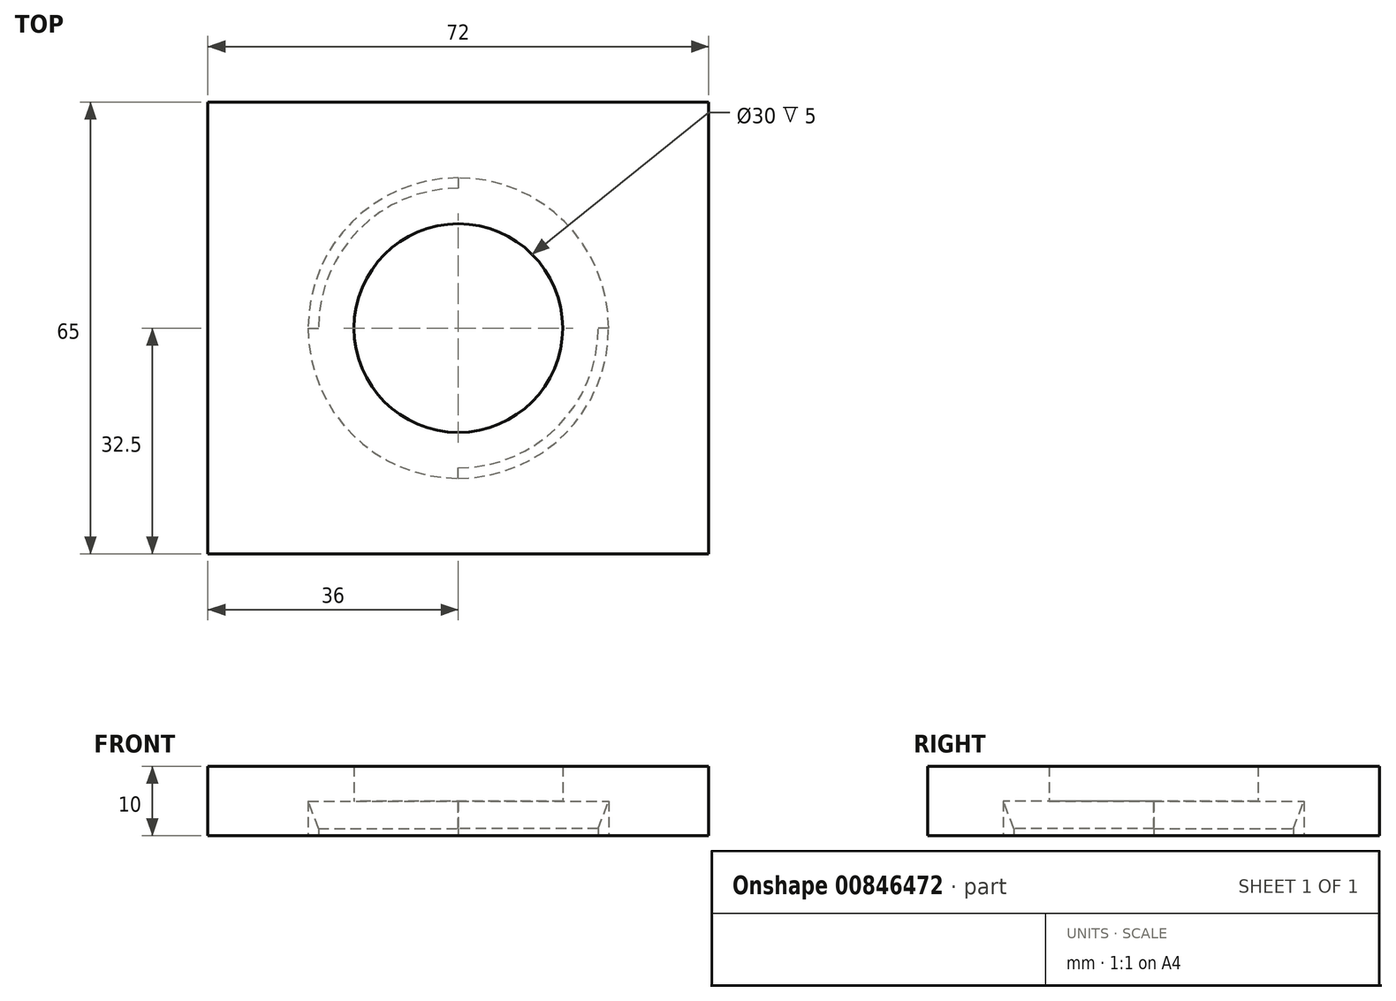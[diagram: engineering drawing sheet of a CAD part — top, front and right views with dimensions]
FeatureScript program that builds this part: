
annotation { "Feature Type Name" : "Feature", "Feature Type Description" : "" }
export const myFeature = defineFeature(function(context is Context, id is Id, definition is map)
    precondition{}
    {
        {
            var Q0;
            Q0=qCreatedBy(makeId("Top.planeOp"),FACE);
            var sketch = newSketch(context, id + "F0", { "sketchPlane" : qUnion([Q0])});
            skLineSegment(sketch, "E0.bottom", {"start": v(36, -32.5) * mm, "end": v(-36, -32.5) * mm});
            skLineSegment(sketch, "E0.top", {"start": v(36, 32.5) * mm, "end": v(-36, 32.5) * mm});
            skLineSegment(sketch, "E0.left", {"start": v(36, -32.5) * mm, "end": v(36, 32.5) * mm});
            skLineSegment(sketch, "E0.right", {"start": v(-36, -32.5) * mm, "end": v(-36, 32.5) * mm});
            skPoint(sketch, "E0.middle", {"position": v(0, 0) * mm});
            skCircle(sketch, "E1", {"center": v(0, 0) * mm, "radius": 15 * mm});
            skSolve(sketch);
        }
        {
            var Q0;
            Q0=makeQuery(id+"F0.imprint","IMPRINT",FACE,{"disambiguationData":[TD([[makeQuery(id+"F0.imprint","IMPRINT",EDGE,{"derivedFrom":sQuery(id+"F0.wireOp",EDGE,"E0.bottom")}),-1.0]])]});
            extrude(context, id + "F1", {"entities" : qUnion([Q0]), "depth" : 10 * mm, "offsetDistance" : 25 * mm});
        }
        {
            var Q0;
            Q0=qCreatedBy(makeId("Right.planeOp"),FACE);
            var sketch = newSketch(context, id + "F2", { "sketchPlane" : qUnion([Q0])});
            skLineSegment(sketch, "E2", {"start": v(0, 0) * mm, "end": v(-20.1, 0) * mm});
            skLineSegment(sketch, "E3", {"start": v(-20.1, 0) * mm, "end": v(-20.1, 1) * mm});
            skLineSegment(sketch, "E4", {"start": v(-20.1, 1) * mm, "end": v(-21.6, 5) * mm});
            skLineSegment(sketch, "E5", {"start": v(-21.6, 5) * mm, "end": v(0, 5) * mm});
            skLineSegment(sketch, "E6", {"start": v(0, 5) * mm, "end": v(0, 0) * mm});
            skSolve(sketch);
        }
        {
            var Q0;
            Q0 = qSketchRegion(id + "F2", true);
            var Q1;
            Q1=sQuery(id+"F2.wireOp",EDGE,"E6");
            revolve(context, id + "F3", {"operationType" : NewBodyOperationType.REMOVE, "surfaceOperationType" : NewSurfaceOperationType.NEW, "entities" : qUnion([Q0]), "axis" : qUnion([Q1]), "revolveType" : RevolveType.FULL, "oppositeDirection" : true});
        }
        {
            var Q0;
            Q0=makeQuery(id+"F1.opExtrude","CAP_FACE",FACE,{"disambiguationData":[OSD([sQuery(id+"F0.wireOp",EDGE,"E0.bottom"),sQuery(id+"F0.wireOp",EDGE,"E0.top"),sQuery(id+"F0.wireOp",EDGE,"E0.left"),sQuery(id+"F0.wireOp",EDGE,"E0.right"),sQuery(id+"F0.wireOp",EDGE,"E1")])],"isStart":true});
            var sketch = newSketch(context, id + "F4", { "sketchPlane" : qUnion([Q0])});
            skArc(sketch, "E7", {"start": v(-21.6, 0) * mm, "mid": v(-15.27, 15.27) * mm, "end": v(0, 21.6) * mm});
            skArc(sketch, "E8", {"start": v(0, -21.6) * mm, "mid": v(15.27, -15.27) * mm, "end": v(21.6, 0) * mm});
            skLineSegment(sketch, "E9", {"start": v(-21.6, 0) * mm, "end": v(-20.1, 0) * mm});
            skLineSegment(sketch, "E10", {"start": v(0, 21.6) * mm, "end": v(0, 20.1) * mm});
            skLineSegment(sketch, "E11", {"start": v(0, -21.6) * mm, "end": v(0, -20.1) * mm});
            skLineSegment(sketch, "E12", {"start": v(21.6, 0) * mm, "end": v(20.1, 0) * mm});
            skArc(sketch, "E13", {"start": v(-20.1, 0) * mm, "mid": v(-14.21, 14.21) * mm, "end": v(0, 20.1) * mm});
            skArc(sketch, "E14", {"start": v(20.1, 0) * mm, "mid": v(14.21, -14.21) * mm, "end": v(0, -20.1) * mm});
            skSolve(sketch);
        }
        {
            var Q0;
            Q0 = qSketchRegion(id + "F4", true);
            extrude(context, id + "F5", {"entities" : qUnion([Q0]), "operationType" : NewBodyOperationType.REMOVE, "oppositeDirection" : true, "depth" : 5 * mm, "offsetDistance" : 25 * mm});
        }
    });
